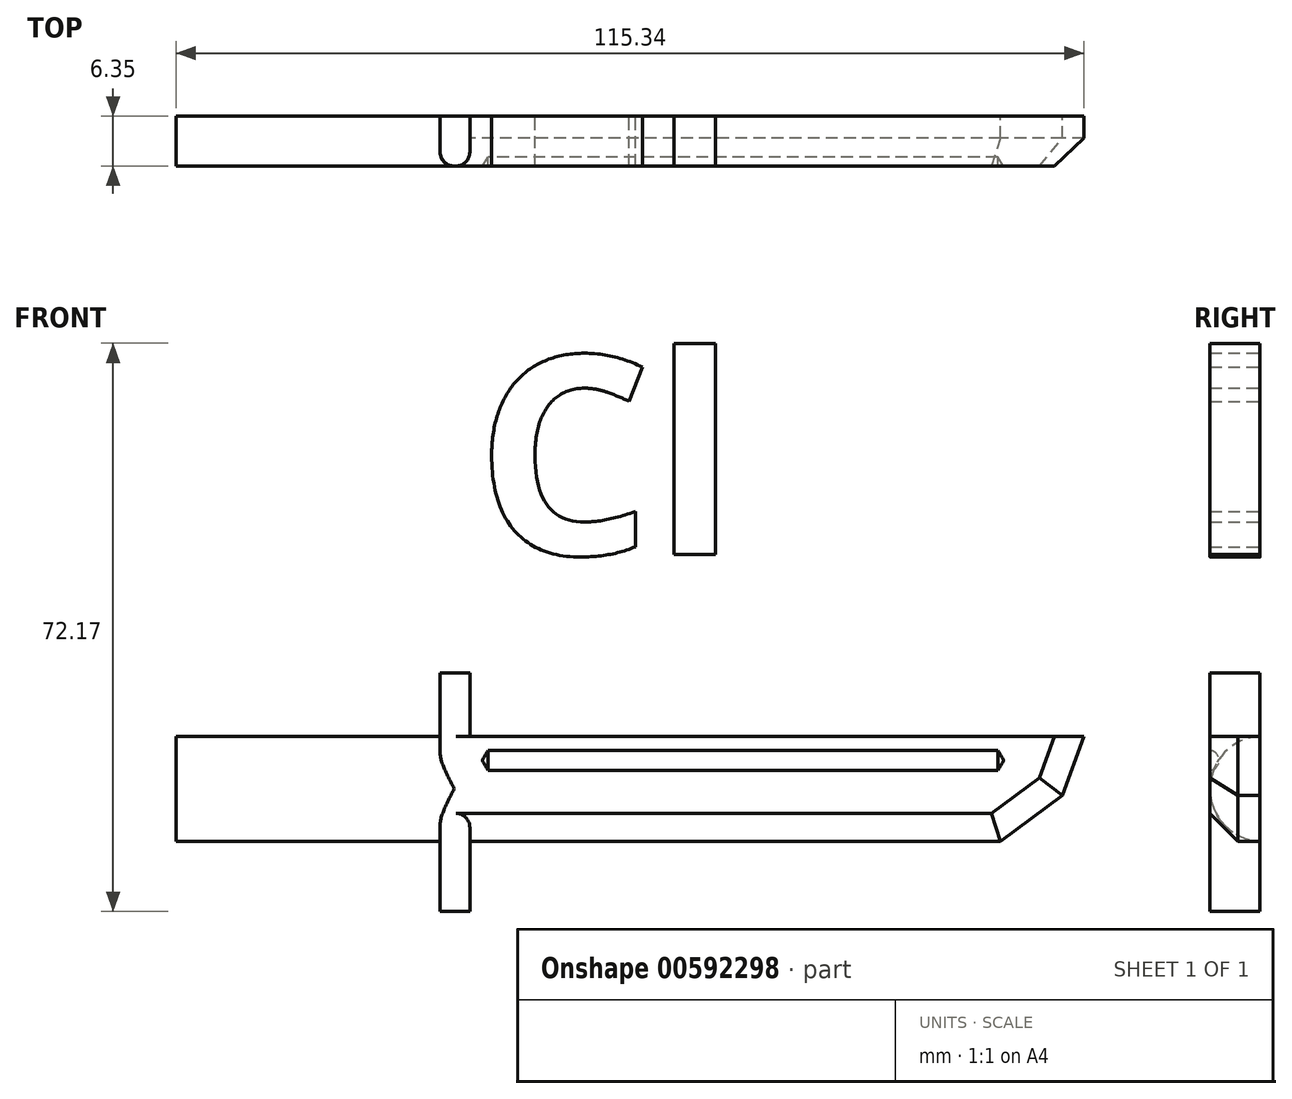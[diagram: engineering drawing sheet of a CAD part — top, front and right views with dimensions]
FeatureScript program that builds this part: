
annotation { "Feature Type Name" : "Feature", "Feature Type Description" : "" }
export const myFeature = defineFeature(function(context is Context, id is Id, definition is map)
    precondition{}
    {
        {
            var Q0;
            Q0=qCreatedBy(makeId("Front.planeOp"),FACE);
            var sketch = newSketch(context, id + "F0", { "sketchPlane" : qUnion([Q0])});
            skText(sketch, "E0", { "text": "Cl", "fontName": "OpenSans-Bold.ttf"});
            skLineSegment(sketch, "E1.bottom", {"start": v(-53.58, -8.01) * mm, "end": v(-20.04, -8.01) * mm});
            skLineSegment(sketch, "E1.top", {"start": v(-53.58, -21.36) * mm, "end": v(-20.04, -21.36) * mm});
            skLineSegment(sketch, "E1.left", {"start": v(-53.58, -8.01) * mm, "end": v(-53.58, -21.36) * mm});
            skLineSegment(sketch, "E1.right", {"start": v(-20.04, -8.01) * mm, "end": v(-20.04, -21.36) * mm});
            skLineSegment(sketch, "E2.bottom", {"start": v(-20.04, 0) * mm, "end": v(-16.27, 0) * mm});
            skLineSegment(sketch, "E2.top", {"start": v(-20.04, -30.26) * mm, "end": v(-16.27, -30.26) * mm});
            skLineSegment(sketch, "E2.left", {"start": v(-20.04, 0) * mm, "end": v(-20.04, -30.26) * mm});
            skLineSegment(sketch, "E2.right", {"start": v(-16.27, 0) * mm, "end": v(-16.27, -30.26) * mm});
            skLineSegment(sketch, "E3", {"start": v(-16.27, -21.36) * mm, "end": v(51.15, -21.36) * mm});
            skLineSegment(sketch, "E4", {"start": v(51.15, -21.36) * mm, "end": v(59.02, -15.54) * mm});
            skLineSegment(sketch, "E5", {"start": v(-16.27, -8.01) * mm, "end": v(61.76, -8.01) * mm});
            skLineSegment(sketch, "E6", {"start": v(61.76, -8.01) * mm, "end": v(59.02, -15.54) * mm});
            skLineSegment(sketch, "E7", {"start": v(-16.27, -11.78) * mm, "end": v(46.7, -11.78) * mm});
            const initialGuessF0  = {"E0": [-0.01555, 0.0151, 1, 0, 0.0254]};
            skSetInitialGuess(sketch, initialGuessF0);
            skSolve(sketch);
        }
        {
            var Q0;
            Q0 = qSketchRegion(id + "F0", true);
            extrude(context, id + "F1", {"entities" : qUnion([Q0]), "depth" : 6.35 * mm, "offsetDistance" : 25.4 * mm});
        }
        {
            var Q0;
            Q0=makeQuery(id+"F1.opExtrude","CAP_EDGE",EDGE,{"disambiguationData":[OSD([sQuery(id+"F0.wireOp",EDGE,"E1.top")])],"isStart":false});
            var Q1;
            Q1=makeQuery(id+"F1.opExtrude","CAP_EDGE",EDGE,{"disambiguationData":[OSD([sQuery(id+"F0.wireOp",EDGE,"E1.bottom")])],"isStart":false});
            fillet(context, id + "F2", {"entities" : qUnion([Q0, Q1]), "radius" : 6.68 * mm, "tangentPropagation" : true, "allowEdgeOverflow" : false});
        }
        {
            var Q0;
            Q0=makeQuery(id+"F1.opExtrude","CAP_EDGE",EDGE,{"disambiguationData":[OSD([sQuery(id+"F0.wireOp",EDGE,"E3")])],"isStart":false});
            var Q1;
            Q1=makeQuery(id+"F1.opExtrude","CAP_EDGE",EDGE,{"disambiguationData":[OSD([sQuery(id+"F0.wireOp",EDGE,"E4")])],"isStart":false});
            var Q2;
            Q2=makeQuery(id+"F1.opExtrude","CAP_EDGE",EDGE,{"disambiguationData":[OSD([sQuery(id+"F0.wireOp",EDGE,"E6")])],"isStart":false});
            chamfer(context, id + "F3", {"entities" : qUnion([Q0, Q1, Q2]), "width" : 3.56 * mm, "tangentPropagation" : true});
        }
        {
            var Q0;
            Q0=qCreatedBy(makeId("Right.planeOp"),FACE);
            var sketch = newSketch(context, id + "F4", { "sketchPlane" : qUnion([Q0])});
            skCircle(sketch, "E8", {"center": v(-6.48, -11.08) * mm, "radius": 1.44 * mm});
            skSolve(sketch);
        }
        {
            var Q0;
            Q0=sQuery(id+"F4.wireOp",VERTEX,"E8.center");
            var Q1;
            Q1=makeQuery(id+"F1.opExtrude","SWEPT_BODY",BODY,{"disambiguationData":[OSD([sQuery(id+"F0.wireOp",EDGE,"E1.bottom"),sQuery(id+"F0.wireOp",EDGE,"E1.top"),sQuery(id+"F0.wireOp",EDGE,"E1.left"),sQuery(id+"F0.wireOp",EDGE,"E2.bottom"),sQuery(id+"F0.wireOp",EDGE,"E2.top"),sQuery(id+"F0.wireOp",EDGE,"E2.left"),sQuery(id+"F0.wireOp",EDGE,"E2.right"),sQuery(id+"F0.wireOp",EDGE,"E3"),sQuery(id+"F0.wireOp",EDGE,"E4"),sQuery(id+"F0.wireOp",EDGE,"E5"),sQuery(id+"F0.wireOp",EDGE,"E6")])]});
            hole(context, id + "F5", {"style" : HoleStyle.SIMPLE, "endStyle" : HoleEndStyle.BLIND, "oppositeDirection" : true, "holeDiameter" : 2.54 * mm, "majorDiameter" : 6.35 * mm, "holeDepth" : 50.8 * mm, "isTappedThrough" : true, "tappedDepth" : 12.7 * mm, "tapClearance" : 3, "locations" : qUnion([Q0]), "scope" : qUnion([Q1])});
        }
        {
            var Q0;
            Q0=sQuery(id+"F4.wireOp",VERTEX,"E8.center");
            var Q1;
            Q1=makeQuery(id+"F1.opExtrude","SWEPT_BODY",BODY,{"disambiguationData":[OSD([sQuery(id+"F0.wireOp",EDGE,"E1.bottom"),sQuery(id+"F0.wireOp",EDGE,"E1.top"),sQuery(id+"F0.wireOp",EDGE,"E1.left"),sQuery(id+"F0.wireOp",EDGE,"E2.bottom"),sQuery(id+"F0.wireOp",EDGE,"E2.top"),sQuery(id+"F0.wireOp",EDGE,"E2.left"),sQuery(id+"F0.wireOp",EDGE,"E2.right"),sQuery(id+"F0.wireOp",EDGE,"E3"),sQuery(id+"F0.wireOp",EDGE,"E4"),sQuery(id+"F0.wireOp",EDGE,"E5"),sQuery(id+"F0.wireOp",EDGE,"E6")])]});
            hole(context, id + "F6", {"style" : HoleStyle.SIMPLE, "endStyle" : HoleEndStyle.BLIND, "holeDiameter" : 2.54 * mm, "majorDiameter" : 6.35 * mm, "holeDepth" : 13.97 * mm, "isTappedThrough" : true, "tappedDepth" : 12.7 * mm, "tapClearance" : 3, "locations" : qUnion([Q0]), "scope" : qUnion([Q1])});
        }
        {
            var Q0;
            {var subQ0=sQuery(id+"F0.wireOp",EDGE,"E2.right");var subQ1=sQuery(id+"F0.wireOp",EDGE,"E2.bottom");var subQ2=sQuery(id+"F0.wireOp",EDGE,"E2.left");Q0=makeQuery(id+"F2.opFillet","BLEND_EDGE",EDGE,{"blendedFrom":[makeQuery(id+"F1.opExtrude","CAP_EDGE",EDGE,{"disambiguationData":[OSD([subQ2]),TDD([makeQuery(id+"F0.imprint","IMPRINT",EDGE,{"disambiguationData":[TD([[makeQuery(id+"F0.imprint","INTERSECT",VERTEX,{"derivedFrom":[sQuery(id+"F0.wireOp",EDGE,"E1.bottom"),subQ2]}),1.0]])],"derivedFrom":subQ2})])],"isStart":false}),makeQuery(id+"F1.opExtrude","SWEPT_FACE",FACE,{"disambiguationData":[OSD([subQ0]),TDD([makeQuery(id+"F0.imprint","IMPRINT",EDGE,{"disambiguationData":[TD([[makeQuery(id+"F0.imprint","INTERSECT",VERTEX,{"derivedFrom":[subQ1,subQ0]}),-1.0]])],"derivedFrom":subQ0})])]})],"blendedInto":[makeQuery(id+"F1.opExtrude","SWEPT_FACE",FACE,{"disambiguationData":[OSD([subQ0]),TDD([makeQuery(id+"F0.imprint","IMPRINT",EDGE,{"disambiguationData":[TD([[makeQuery(id+"F0.imprint","INTERSECT",VERTEX,{"derivedFrom":[subQ1,subQ0]}),-1.0]])],"derivedFrom":subQ0})])]})]});}
            var Q1;
            {var subQ0=sQuery(id+"F0.wireOp",EDGE,"E2.right");var subQ1=sQuery(id+"F0.wireOp",EDGE,"E2.top");var subQ2=sQuery(id+"F0.wireOp",EDGE,"E2.left");Q1=makeQuery(id+"F2.opFillet","BLEND_EDGE",EDGE,{"blendedFrom":[makeQuery(id+"F1.opExtrude","CAP_EDGE",EDGE,{"disambiguationData":[OSD([subQ2]),TDD([makeQuery(id+"F0.imprint","IMPRINT",EDGE,{"disambiguationData":[TD([[makeQuery(id+"F0.imprint","INTERSECT",VERTEX,{"derivedFrom":[sQuery(id+"F0.wireOp",EDGE,"E1.top"),subQ2]}),-1.0]])],"derivedFrom":subQ2})])],"isStart":false}),makeQuery(id+"F1.opExtrude","SWEPT_FACE",FACE,{"disambiguationData":[OSD([subQ0]),TDD([makeQuery(id+"F0.imprint","IMPRINT",EDGE,{"disambiguationData":[TD([[makeQuery(id+"F0.imprint","INTERSECT",VERTEX,{"derivedFrom":[subQ1,subQ0]}),1.0]])],"derivedFrom":subQ0})])]})],"blendedInto":[makeQuery(id+"F1.opExtrude","SWEPT_FACE",FACE,{"disambiguationData":[OSD([subQ0]),TDD([makeQuery(id+"F0.imprint","IMPRINT",EDGE,{"disambiguationData":[TD([[makeQuery(id+"F0.imprint","INTERSECT",VERTEX,{"derivedFrom":[subQ1,subQ0]}),1.0]])],"derivedFrom":subQ0})])]})]});}
            var Q2;
            {var subQ0=sQuery(id+"F0.wireOp",EDGE,"E2.right");Q2=makeQuery(id+"F1.opExtrude","CAP_EDGE",EDGE,{"disambiguationData":[OSD([subQ0]),TDD([makeQuery(id+"F0.imprint","IMPRINT",EDGE,{"disambiguationData":[TD([[makeQuery(id+"F0.imprint","INTERSECT",VERTEX,{"derivedFrom":[sQuery(id+"F0.wireOp",EDGE,"E2.bottom"),subQ0]}),-1.0]])],"derivedFrom":subQ0})])],"isStart":false});}
            var Q3;
            {var subQ0=sQuery(id+"F0.wireOp",EDGE,"E2.right");Q3=makeQuery(id+"F1.opExtrude","CAP_EDGE",EDGE,{"disambiguationData":[OSD([subQ0]),TDD([makeQuery(id+"F0.imprint","IMPRINT",EDGE,{"disambiguationData":[TD([[makeQuery(id+"F0.imprint","INTERSECT",VERTEX,{"derivedFrom":[sQuery(id+"F0.wireOp",EDGE,"E2.top"),subQ0]}),1.0]])],"derivedFrom":subQ0})])],"isStart":false});}
            var Q4;
            {var subQ0=sQuery(id+"F0.wireOp",EDGE,"E2.left");Q4=makeQuery(id+"F1.opExtrude","CAP_EDGE",EDGE,{"disambiguationData":[OSD([subQ0]),TDD([makeQuery(id+"F0.imprint","IMPRINT",EDGE,{"disambiguationData":[TD([[makeQuery(id+"F0.imprint","INTERSECT",VERTEX,{"derivedFrom":[sQuery(id+"F0.wireOp",EDGE,"E1.bottom"),subQ0]}),1.0]])],"derivedFrom":subQ0})])],"isStart":false});}
            var Q5;
            {var subQ0=sQuery(id+"F0.wireOp",EDGE,"E2.left");Q5=makeQuery(id+"F1.opExtrude","CAP_EDGE",EDGE,{"disambiguationData":[OSD([subQ0]),TDD([makeQuery(id+"F0.imprint","IMPRINT",EDGE,{"disambiguationData":[TD([[makeQuery(id+"F0.imprint","INTERSECT",VERTEX,{"derivedFrom":[sQuery(id+"F0.wireOp",EDGE,"E1.top"),subQ0]}),-1.0]])],"derivedFrom":subQ0})])],"isStart":false});}
            fillet(context, id + "F7", {"entities" : qUnion([Q0, Q1, Q2, Q3, Q4, Q5]), "radius" : 1.78 * mm, "tangentPropagation" : true, "allowEdgeOverflow" : false});
        }
    });
